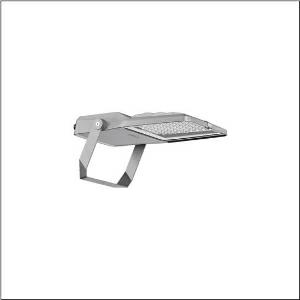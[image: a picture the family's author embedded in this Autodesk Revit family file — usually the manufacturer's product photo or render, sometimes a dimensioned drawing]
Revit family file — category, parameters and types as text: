
# Revit family: floodlight_fl_21_mini___pl43_5xa7774c2a1a_b50a
name_source: partatom
category: Lighting Fixtures
units: mm (PartAtom-declared; Revit-internal decimal feet)

## family parameters
Cut with Voids When Loaded = No
Host = Face
Light Source = No
Part Type = Normal
Room Calculation Point = No
Round Connector Dimension = Use Diameter
Shared = No

## types (1)
- --- (1 x LED, 12480 lm, 88.8 W, 3000K)
    Apparent Load = 89 VA
    CIE Flux Codes = 27 78 99 100 100
    Color Rendering = 70
    Color Temperature = 3000K
    Default Elevation = 1800 mm
    Description = Floodlight FL 21 mini, floodlight, primary light control with lens, of PMMA, primary optical cover: protective disc, of toughened safety glass, transparent, light distribution: PL43, light emission: direct distribution, installation type: surface-mounted, LED, High Power LED, rated luminous flux: 12.480lm, luminous efficacy: 141lm/W, light colour: 730, colour temperature: 3000K, control gear: DALI 2, control: overheat protection, power reduction, constant luminous flux control, flexible luminous flux parameterisation, with terminal, 6-pole, mains connection: 220..240V, AC/DC, 0/50..60Hz, start of lifetime: 89W, end of service life: 94W, reduction: 42W, luminaire housing, of diecast aluminium, powder-coated, Siteco® metallic grey (DB 702S), corrosivity category C5 mid according to DIN EN ISO 12944, chlorine-resistant, suitable for swimming pools, sealing non-destructively replaceable, mounting bracket, of steel, galvanised, powder-coated, Siteco® metallic grey (DB 702S), protection rating (complete): IP66, insulation class (complete): insulation class II (safety insulation), certification: CE, ENEC, VDE, impact resistance: IK08, permissible operating ambient temperature: -40..+40°C, permissible operating ambient temperature for outdoor applications: -40..+50°C, standard: DIN EN 12944, LABS conformity tested according to VDMA 24364:2018-05, packaging unit: 1 piece

Light Distribution: PL43
    Height = 70 mm
    Lamp = 1 x LED
    Lamp Light Flux = 12480 lm
    Lamp Power = 88.8 W
    Lamp count = 1
    Length = 485 mm
    Luminous efficacy = 141 lm/W
    Manufacturer = Siteco
    ModVariant = No
    Model = 5XA7774C2A1A
    Number of Poles = 1
    OnlyDefault = Yes
    Power Factor = 1
    Product Name = Floodlight FL 21 mini | PL43
    Product group = floodlight | pylon annexe
    ProductGroupID = 6201
    Protection Class = Protection class II
    Protection Degree = IP 66
    RLX_Detail_Level = 1
    RLX_Emergency_Light_Flux = 0 lm
    RLX_Emergency_Type = 0
    RLX_Emergency_Type_DB = No
    RlxData = <blob elided: 95973 chars, md5=47fcdc70>
    Socket = socket
    Standby Power = 0 W
    System Light Flux = 12480 lm
    System Power = 89 W
    Type Comments = factory setting: luminous flux: 100 % | dim-lin: 254 | 456 mA
    Type Image = l_1006845.jpg
    URL = http://relux.com
    VarID = @adj_183683
    Voltage = 0 V
    Weight = 0.00 kg
    Width = 337 mm

## geometry (parser evidence)
native form markers: Blend x4, Sweep x13
no freeform markers — native parametric forms only
